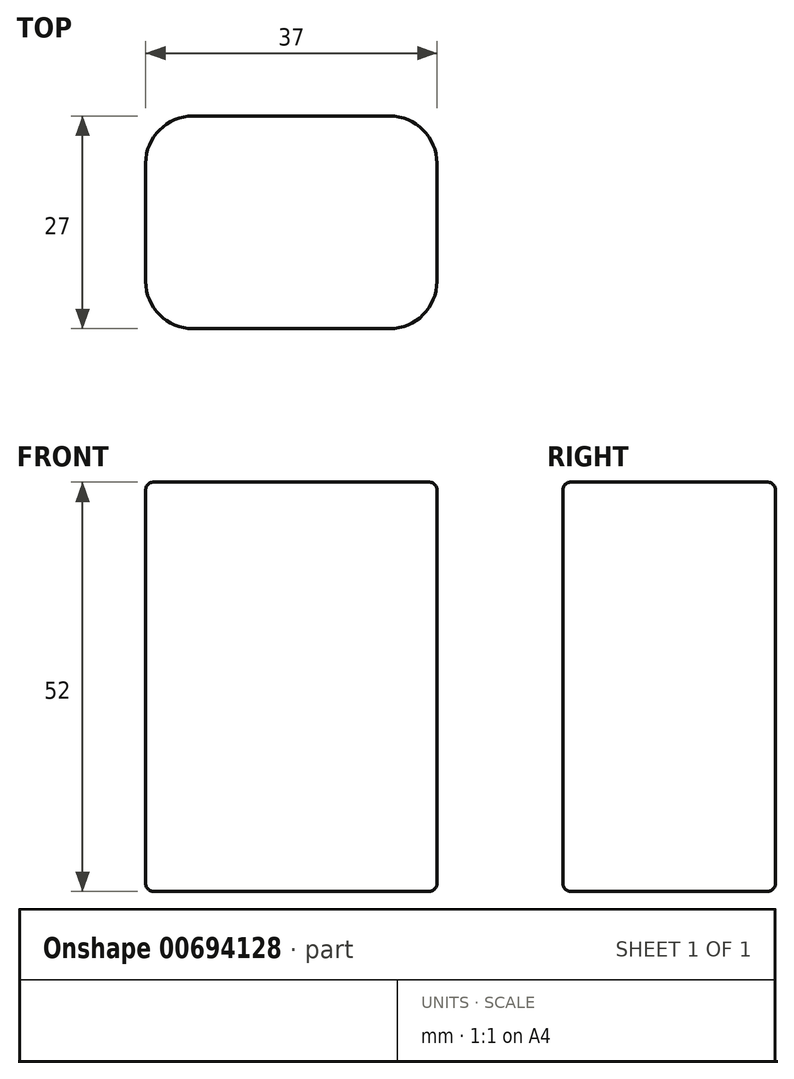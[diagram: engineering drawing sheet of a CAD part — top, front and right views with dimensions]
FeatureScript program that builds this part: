
annotation { "Feature Type Name" : "Feature", "Feature Type Description" : "" }
export const myFeature = defineFeature(function(context is Context, id is Id, definition is map)
    precondition{}
    {
        {
            var Q0;
            Q0=qCreatedBy(makeId("Top.planeOp"),FACE);
            var sketch = newSketch(context, id + "F0", { "sketchPlane" : qUnion([Q0])});
            skLineSegment(sketch, "E0.bottom", {"start": v(18.5, -13.5) * mm, "end": v(-18.5, -13.5) * mm});
            skLineSegment(sketch, "E0.top", {"start": v(18.5, 13.5) * mm, "end": v(-18.5, 13.5) * mm});
            skLineSegment(sketch, "E0.left", {"start": v(18.5, -13.5) * mm, "end": v(18.5, 13.5) * mm});
            skLineSegment(sketch, "E0.right", {"start": v(-18.5, -13.5) * mm, "end": v(-18.5, 13.5) * mm});
            skPoint(sketch, "E0.middle", {"position": v(0, 0) * mm});
            skSolve(sketch);
        }
        {
            var Q0;
            Q0=makeQuery(id+"F0.imprint","IMPRINT",FACE,{"disambiguationData":[TD([[makeQuery(id+"F0.imprint","IMPRINT",EDGE,{"derivedFrom":sQuery(id+"F0.wireOp",EDGE,"E0.bottom")}),-1.0]])]});
            extrude(context, id + "F1", {"entities" : qUnion([Q0]), "depth" : 52 * mm, "offsetDistance" : 25 * mm});
        }
        {
            var Q0;
            Q0=makeQuery(id+"F1.opExtrude","SWEPT_EDGE",EDGE,{"disambiguationData":[OSD([sQuery(id+"F0.wireOp",EDGE,"E0.bottom"),sQuery(id+"F0.wireOp",EDGE,"E0.left")])]});
            var Q1;
            Q1=makeQuery(id+"F1.opExtrude","SWEPT_EDGE",EDGE,{"disambiguationData":[OSD([sQuery(id+"F0.wireOp",EDGE,"E0.top"),sQuery(id+"F0.wireOp",EDGE,"E0.left")])]});
            var Q2;
            Q2=makeQuery(id+"F1.opExtrude","SWEPT_EDGE",EDGE,{"disambiguationData":[OSD([sQuery(id+"F0.wireOp",EDGE,"E0.bottom"),sQuery(id+"F0.wireOp",EDGE,"E0.right")])]});
            var Q3;
            Q3=makeQuery(id+"F1.opExtrude","SWEPT_EDGE",EDGE,{"disambiguationData":[OSD([sQuery(id+"F0.wireOp",EDGE,"E0.top"),sQuery(id+"F0.wireOp",EDGE,"E0.right")])]});
            fillet(context, id + "F2", {"entities" : qUnion([Q0, Q1, Q2, Q3]), "radius" : 6 * mm, "tangentPropagation" : true, "allowEdgeOverflow" : false});
        }
        {
            var Q0;
            Q0=makeQuery(id+"F1.opExtrude","CAP_EDGE",EDGE,{"disambiguationData":[OSD([sQuery(id+"F0.wireOp",EDGE,"E0.bottom")])],"isStart":false});
            var Q1;
            {var subQ0=sQuery(id+"F0.wireOp",EDGE,"E0.right");var subQ1=sQuery(id+"F0.wireOp",EDGE,"E0.bottom");Q1=makeQuery(id+"F2.opFillet","BLEND_EDGE",EDGE,{"blendedFrom":[makeQuery(id+"F1.opExtrude","SWEPT_EDGE",EDGE,{"disambiguationData":[OSD([subQ1,subQ0])]}),makeQuery(id+"F1.opExtrude","CAP_FACE",FACE,{"disambiguationData":[OSD([subQ1,sQuery(id+"F0.wireOp",EDGE,"E0.top"),sQuery(id+"F0.wireOp",EDGE,"E0.left"),subQ0])],"isStart":false})],"blendedInto":[makeQuery(id+"F1.opExtrude","CAP_FACE",FACE,{"disambiguationData":[OSD([subQ1,sQuery(id+"F0.wireOp",EDGE,"E0.top"),sQuery(id+"F0.wireOp",EDGE,"E0.left"),subQ0])],"isStart":false})]});}
            var Q2;
            Q2=makeQuery(id+"F1.opExtrude","CAP_EDGE",EDGE,{"disambiguationData":[OSD([sQuery(id+"F0.wireOp",EDGE,"E0.right")])],"isStart":false});
            var Q3;
            {var subQ0=sQuery(id+"F0.wireOp",EDGE,"E0.right");var subQ1=sQuery(id+"F0.wireOp",EDGE,"E0.top");Q3=makeQuery(id+"F2.opFillet","BLEND_EDGE",EDGE,{"blendedFrom":[makeQuery(id+"F1.opExtrude","SWEPT_EDGE",EDGE,{"disambiguationData":[OSD([subQ1,subQ0])]}),makeQuery(id+"F1.opExtrude","CAP_FACE",FACE,{"disambiguationData":[OSD([sQuery(id+"F0.wireOp",EDGE,"E0.bottom"),subQ1,sQuery(id+"F0.wireOp",EDGE,"E0.left"),subQ0])],"isStart":false})],"blendedInto":[makeQuery(id+"F1.opExtrude","CAP_FACE",FACE,{"disambiguationData":[OSD([sQuery(id+"F0.wireOp",EDGE,"E0.bottom"),subQ1,sQuery(id+"F0.wireOp",EDGE,"E0.left"),subQ0])],"isStart":false})]});}
            var Q4;
            Q4=makeQuery(id+"F1.opExtrude","CAP_EDGE",EDGE,{"disambiguationData":[OSD([sQuery(id+"F0.wireOp",EDGE,"E0.top")])],"isStart":false});
            var Q5;
            {var subQ0=sQuery(id+"F0.wireOp",EDGE,"E0.left");var subQ1=sQuery(id+"F0.wireOp",EDGE,"E0.top");Q5=makeQuery(id+"F2.opFillet","BLEND_EDGE",EDGE,{"blendedFrom":[makeQuery(id+"F1.opExtrude","SWEPT_EDGE",EDGE,{"disambiguationData":[OSD([subQ1,subQ0])]}),makeQuery(id+"F1.opExtrude","CAP_FACE",FACE,{"disambiguationData":[OSD([sQuery(id+"F0.wireOp",EDGE,"E0.bottom"),subQ1,subQ0,sQuery(id+"F0.wireOp",EDGE,"E0.right")])],"isStart":false})],"blendedInto":[makeQuery(id+"F1.opExtrude","CAP_FACE",FACE,{"disambiguationData":[OSD([sQuery(id+"F0.wireOp",EDGE,"E0.bottom"),subQ1,subQ0,sQuery(id+"F0.wireOp",EDGE,"E0.right")])],"isStart":false})]});}
            var Q6;
            Q6=makeQuery(id+"F1.opExtrude","CAP_EDGE",EDGE,{"disambiguationData":[OSD([sQuery(id+"F0.wireOp",EDGE,"E0.left")])],"isStart":false});
            var Q7;
            {var subQ0=sQuery(id+"F0.wireOp",EDGE,"E0.left");var subQ1=sQuery(id+"F0.wireOp",EDGE,"E0.bottom");Q7=makeQuery(id+"F2.opFillet","BLEND_EDGE",EDGE,{"blendedFrom":[makeQuery(id+"F1.opExtrude","SWEPT_EDGE",EDGE,{"disambiguationData":[OSD([subQ1,subQ0])]}),makeQuery(id+"F1.opExtrude","CAP_FACE",FACE,{"disambiguationData":[OSD([subQ1,sQuery(id+"F0.wireOp",EDGE,"E0.top"),subQ0,sQuery(id+"F0.wireOp",EDGE,"E0.right")])],"isStart":false})],"blendedInto":[makeQuery(id+"F1.opExtrude","CAP_FACE",FACE,{"disambiguationData":[OSD([subQ1,sQuery(id+"F0.wireOp",EDGE,"E0.top"),subQ0,sQuery(id+"F0.wireOp",EDGE,"E0.right")])],"isStart":false})]});}
            var Q8;
            {var subQ0=sQuery(id+"F0.wireOp",EDGE,"E0.left");var subQ1=sQuery(id+"F0.wireOp",EDGE,"E0.bottom");Q8=makeQuery(id+"F2.opFillet","BLEND_EDGE",EDGE,{"blendedFrom":[makeQuery(id+"F1.opExtrude","SWEPT_EDGE",EDGE,{"disambiguationData":[OSD([subQ1,subQ0])]}),makeQuery(id+"F1.opExtrude","CAP_FACE",FACE,{"disambiguationData":[OSD([subQ1,sQuery(id+"F0.wireOp",EDGE,"E0.top"),subQ0,sQuery(id+"F0.wireOp",EDGE,"E0.right")])],"isStart":true})],"blendedInto":[makeQuery(id+"F1.opExtrude","CAP_FACE",FACE,{"disambiguationData":[OSD([subQ1,sQuery(id+"F0.wireOp",EDGE,"E0.top"),subQ0,sQuery(id+"F0.wireOp",EDGE,"E0.right")])],"isStart":true})]});}
            var Q9;
            Q9=makeQuery(id+"F1.opExtrude","CAP_EDGE",EDGE,{"disambiguationData":[OSD([sQuery(id+"F0.wireOp",EDGE,"E0.left")])],"isStart":true});
            var Q10;
            {var subQ0=sQuery(id+"F0.wireOp",EDGE,"E0.left");var subQ1=sQuery(id+"F0.wireOp",EDGE,"E0.top");Q10=makeQuery(id+"F2.opFillet","BLEND_EDGE",EDGE,{"blendedFrom":[makeQuery(id+"F1.opExtrude","SWEPT_EDGE",EDGE,{"disambiguationData":[OSD([subQ1,subQ0])]}),makeQuery(id+"F1.opExtrude","CAP_FACE",FACE,{"disambiguationData":[OSD([sQuery(id+"F0.wireOp",EDGE,"E0.bottom"),subQ1,subQ0,sQuery(id+"F0.wireOp",EDGE,"E0.right")])],"isStart":true})],"blendedInto":[makeQuery(id+"F1.opExtrude","CAP_FACE",FACE,{"disambiguationData":[OSD([sQuery(id+"F0.wireOp",EDGE,"E0.bottom"),subQ1,subQ0,sQuery(id+"F0.wireOp",EDGE,"E0.right")])],"isStart":true})]});}
            var Q11;
            Q11=makeQuery(id+"F1.opExtrude","CAP_EDGE",EDGE,{"disambiguationData":[OSD([sQuery(id+"F0.wireOp",EDGE,"E0.top")])],"isStart":true});
            var Q12;
            {var subQ0=sQuery(id+"F0.wireOp",EDGE,"E0.right");var subQ1=sQuery(id+"F0.wireOp",EDGE,"E0.top");Q12=makeQuery(id+"F2.opFillet","BLEND_EDGE",EDGE,{"blendedFrom":[makeQuery(id+"F1.opExtrude","SWEPT_EDGE",EDGE,{"disambiguationData":[OSD([subQ1,subQ0])]}),makeQuery(id+"F1.opExtrude","CAP_FACE",FACE,{"disambiguationData":[OSD([sQuery(id+"F0.wireOp",EDGE,"E0.bottom"),subQ1,sQuery(id+"F0.wireOp",EDGE,"E0.left"),subQ0])],"isStart":true})],"blendedInto":[makeQuery(id+"F1.opExtrude","CAP_FACE",FACE,{"disambiguationData":[OSD([sQuery(id+"F0.wireOp",EDGE,"E0.bottom"),subQ1,sQuery(id+"F0.wireOp",EDGE,"E0.left"),subQ0])],"isStart":true})]});}
            var Q13;
            Q13=makeQuery(id+"F1.opExtrude","CAP_EDGE",EDGE,{"disambiguationData":[OSD([sQuery(id+"F0.wireOp",EDGE,"E0.right")])],"isStart":true});
            var Q14;
            {var subQ0=sQuery(id+"F0.wireOp",EDGE,"E0.right");var subQ1=sQuery(id+"F0.wireOp",EDGE,"E0.bottom");Q14=makeQuery(id+"F2.opFillet","BLEND_EDGE",EDGE,{"blendedFrom":[makeQuery(id+"F1.opExtrude","SWEPT_EDGE",EDGE,{"disambiguationData":[OSD([subQ1,subQ0])]}),makeQuery(id+"F1.opExtrude","CAP_FACE",FACE,{"disambiguationData":[OSD([subQ1,sQuery(id+"F0.wireOp",EDGE,"E0.top"),sQuery(id+"F0.wireOp",EDGE,"E0.left"),subQ0])],"isStart":true})],"blendedInto":[makeQuery(id+"F1.opExtrude","CAP_FACE",FACE,{"disambiguationData":[OSD([subQ1,sQuery(id+"F0.wireOp",EDGE,"E0.top"),sQuery(id+"F0.wireOp",EDGE,"E0.left"),subQ0])],"isStart":true})]});}
            var Q15;
            Q15=makeQuery(id+"F1.opExtrude","CAP_EDGE",EDGE,{"disambiguationData":[OSD([sQuery(id+"F0.wireOp",EDGE,"E0.bottom")])],"isStart":true});
            fillet(context, id + "F3", {"entities" : qUnion([Q0, Q1, Q2, Q3, Q4, Q5, Q6, Q7, Q8, Q9, Q10, Q11, Q12, Q13, Q14, Q15]), "radius" : 1 * mm, "tangentPropagation" : true, "allowEdgeOverflow" : false});
        }
    });
